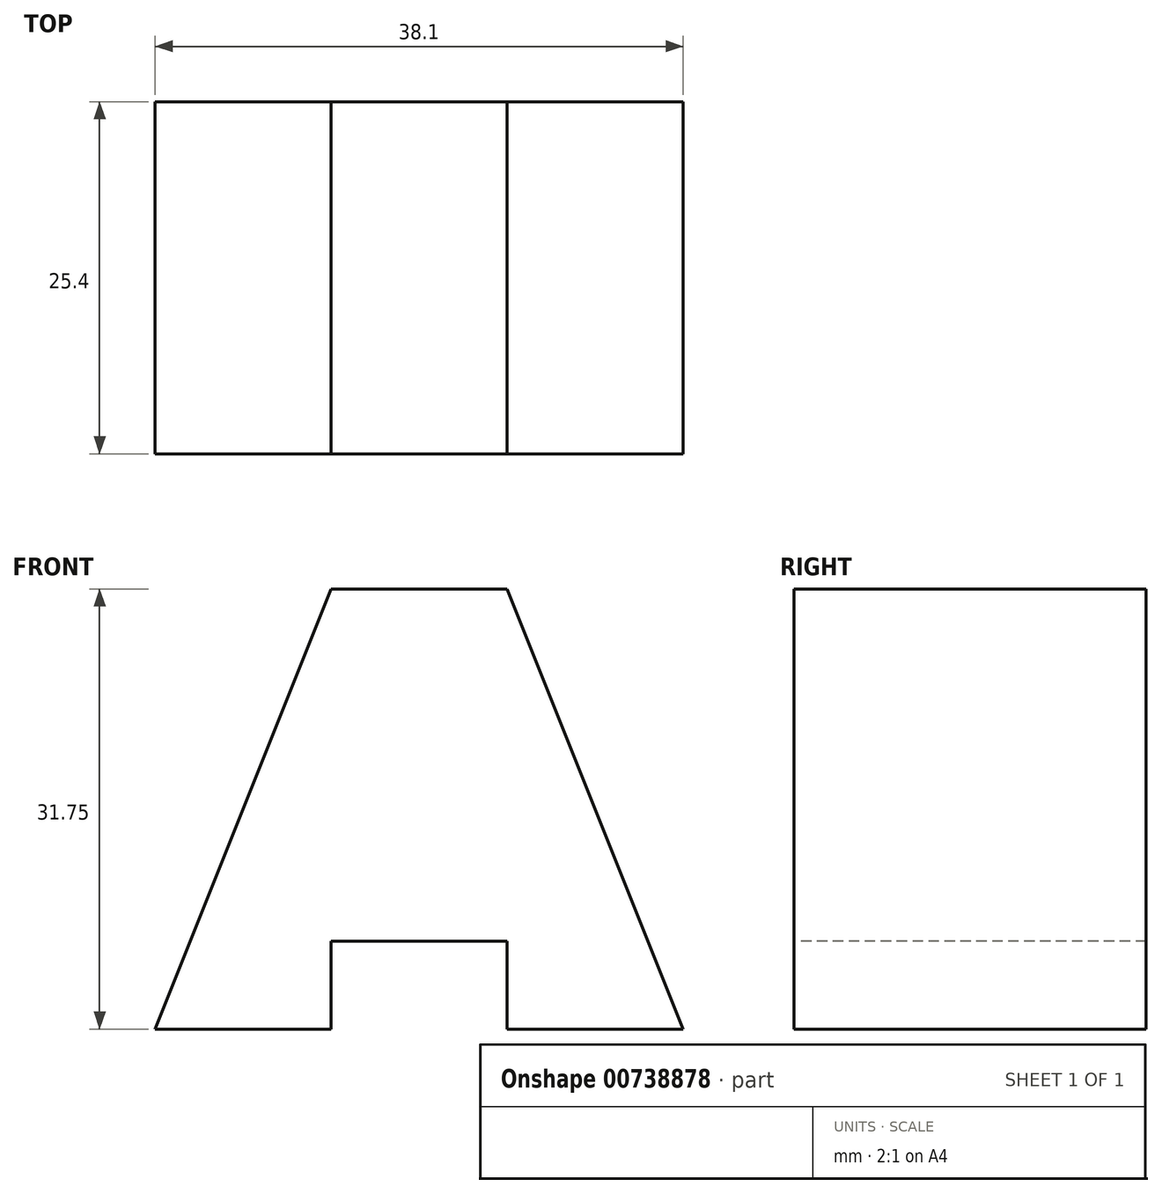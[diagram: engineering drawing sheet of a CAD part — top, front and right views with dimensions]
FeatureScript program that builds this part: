
annotation { "Feature Type Name" : "Feature", "Feature Type Description" : "" }
export const myFeature = defineFeature(function(context is Context, id is Id, definition is map)
    precondition{}
    {
        {
            var Q0;
            Q0=qCreatedBy(makeId("Front.planeOp"),FACE);
            var sketch = newSketch(context, id + "F0", { "sketchPlane" : qUnion([Q0])});
            skLineSegment(sketch, "E0", {"start": v(0, 31.75) * mm, "end": v(0, 0) * mm});
            skLineSegment(sketch, "E1", {"start": v(0, 0) * mm, "end": v(38.1, 0) * mm});
            skLineSegment(sketch, "E2", {"start": v(38.1, 0) * mm, "end": v(38.1, 31.75) * mm});
            skLineSegment(sketch, "E3", {"start": v(38.1, 31.75) * mm, "end": v(0, 31.75) * mm});
            skSolve(sketch);
        }
        {
            var Q0;
            Q0=makeQuery(id+"F0.imprint","IMPRINT",FACE,{"disambiguationData":[TD([[makeQuery(id+"F0.imprint","IMPRINT",EDGE,{"derivedFrom":sQuery(id+"F0.wireOp",EDGE,"E0")}),1.0]])]});
            extrude(context, id + "F1", {"entities" : qUnion([Q0]), "depth" : 25.4 * mm, "offsetDistance" : 25.4 * mm});
        }
        {
            var Q0;
            Q0=makeQuery(id+"F1.opExtrude","CAP_FACE",FACE,{"disambiguationData":[OSD([sQuery(id+"F0.wireOp",EDGE,"E0"),sQuery(id+"F0.wireOp",EDGE,"E1"),sQuery(id+"F0.wireOp",EDGE,"E2"),sQuery(id+"F0.wireOp",EDGE,"E3")])],"isStart":false});
            var sketch = newSketch(context, id + "F2", { "sketchPlane" : qUnion([Q0])});
            skLineSegment(sketch, "E4", {"start": v(12.7, 31.75) * mm, "end": v(0, 0) * mm});
            skLineSegment(sketch, "E5", {"start": v(25.4, 31.75) * mm, "end": v(38.1, 0) * mm});
            skLineSegment(sketch, "E6", {"start": v(25.4, 31.75) * mm, "end": v(38.1, 31.75) * mm});
            skLineSegment(sketch, "E7", {"start": v(12.7, 31.75) * mm, "end": v(0, 31.75) * mm});
            skLineSegment(sketch, "E8", {"start": v(12.7, 0) * mm, "end": v(12.7, 6.35) * mm});
            skLineSegment(sketch, "E9", {"start": v(25.4, 0) * mm, "end": v(25.4, 6.35) * mm});
            skLineSegment(sketch, "E10", {"start": v(12.7, 6.35) * mm, "end": v(25.4, 6.35) * mm});
            skSolve(sketch);
        }
        {
            var Q0;
            Q0 = qSketchRegion(id + "F2", true);
            var Q1;
            Q1=makeQuery(id+"F2.imprint","IMPRINT",FACE,{"disambiguationData":[TD([[makeQuery(id+"F2.imprint","IMPRINT",EDGE,{"derivedFrom":sQuery(id+"F2.wireOp",EDGE,"E4")}),-1.0]])]});
            var Q2;
            Q2=makeQuery(id+"F2.imprint","IMPRINT",FACE,{"disambiguationData":[TD([[makeQuery(id+"F2.imprint","IMPRINT",EDGE,{"derivedFrom":sQuery(id+"F2.wireOp",EDGE,"E5")}),1.0]])]});
            var Q3;
            {var subQ0=sQuery(id+"F2.wireOp",EDGE,"E8");Q3=makeQuery(id+"F2.imprint","IMPRINT",FACE,{"disambiguationData":[TD([[makeQuery(id+"F2.imprint","IMPRINT",EDGE,{"derivedFrom":subQ0}),-1.0]])]});}
            extrude(context, id + "F3", {"entities" : qUnion([Q0, Q1, Q2, Q3]), "operationType" : NewBodyOperationType.REMOVE, "endBound" : BoundingType.THROUGH_ALL, "oppositeDirection" : true, "depth" : 25.4 * mm, "offsetDistance" : 25.4 * mm});
        }
    });
